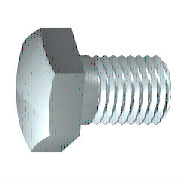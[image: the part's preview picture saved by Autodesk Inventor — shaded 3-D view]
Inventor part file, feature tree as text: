
AUTODESK INVENTOR PART (.ipt)
format: ipt  version: 2023.1 (Build 271208000, 208)  size: 194,048 bytes
history: native  units: mm (DEFAULTED — no unit token found)
features: sketch x3, extrude x1, chamfer x1, plane x1
ambient origin geometry x7: Origin, YZ Plane, XZ Plane, X Axis, Y Axis, Z Axis, Center Point
bodies: Solid1 (feature_tree), Body (feature_tree)
feature tree (6):
  extrude  "Head"  Depth=21.0mm
  chamfer  "Chamfer1"  Distance=7.6mm
  plane  "Work Plane1"
  sketch  "Sketch1"  dims[d0=30.0mm d1=21.0mm]
  sketch  "Sketch2"  dims[d2=12.0mm]
  sketch  "Sketch4"  dims[d12=90.0deg d3=7.6mm d4=0.0mm d5=30.0deg d21=90.0deg d6=1.073538mm d7=1.073638mm d8=0.0mm d9=0.4001mm d10=20.0mm d11=22.0mm d13=1.073638mm d14=12.0mm d15=21.0mm d16=0.0mm d19=22.0mm d55=45.0deg d57=0.0mm d58=0.0mm]
